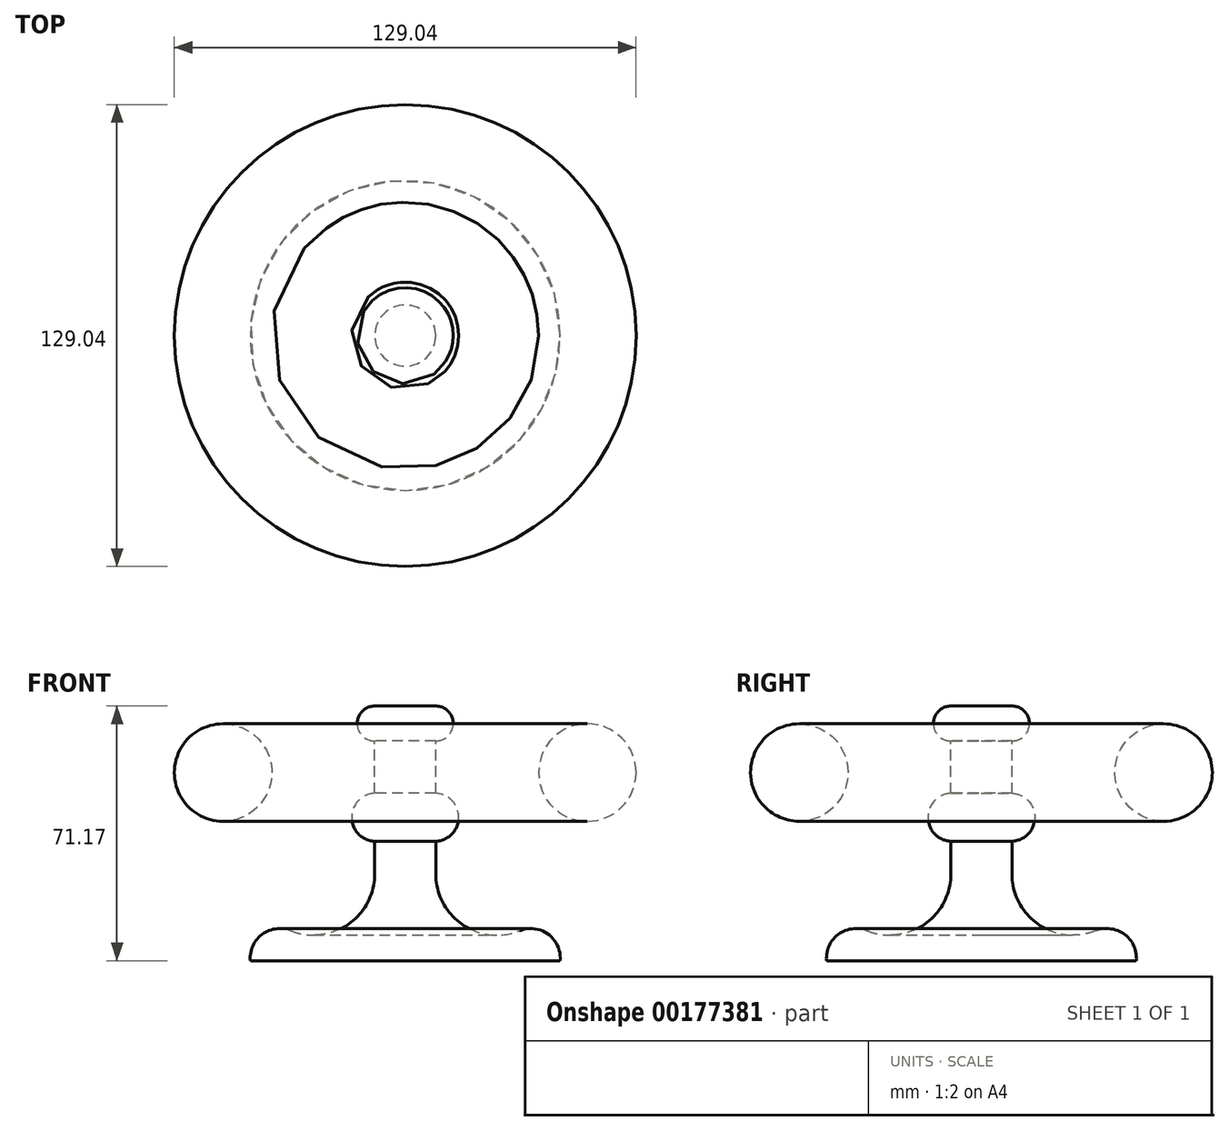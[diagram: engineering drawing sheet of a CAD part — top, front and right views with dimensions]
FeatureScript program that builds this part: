
annotation { "Feature Type Name" : "Feature", "Feature Type Description" : "" }
export const myFeature = defineFeature(function(context is Context, id is Id, definition is map)
    precondition{}
    {
        {
            var Q0;
            Q0=qCreatedBy(makeId("Front.planeOp"),FACE);
            var sketch = newSketch(context, id + "F0", { "sketchPlane" : qUnion([Q0])});
            skLineSegment(sketch, "E0", {"start": v(0, 71.17) * mm, "end": v(0, 0) * mm});
            skLineSegment(sketch, "E1", {"start": v(0, 0) * mm, "end": v(43.28, 0) * mm});
            skLineSegment(sketch, "E2", {"start": v(0, 71.17) * mm, "end": v(8.53, 71.17) * mm});
            skArc(sketch, "E3", {"start": v(8.53, 61.42) * mm, "mid": v(13.41, 66.3) * mm, "end": v(8.53, 71.17) * mm});
            skLineSegment(sketch, "E4", {"start": v(8.53, 61.42) * mm, "end": v(8.53, 46.79) * mm});
            skArc(sketch, "E5", {"start": v(8.53, 33.38) * mm, "mid": v(14.94, 40.08) * mm, "end": v(8.53, 46.79) * mm});
            skLineSegment(sketch, "E6", {"start": v(8.53, 33.38) * mm, "end": v(8.53, 24.23) * mm});
            skArc(sketch, "E7", {"start": v(8.53, 24.23) * mm, "mid": v(16.06, 10.07) * mm, "end": v(32, 8.38) * mm});
            skArc(sketch, "E8", {"start": v(32, 8.38) * mm, "mid": v(40, 7.35) * mm, "end": v(43.28, 0) * mm});
            skLineSegment(sketch, "E9", {"start": v(0, 97.69) * mm, "end": v(0, -25.15) * mm});
            skSolve(sketch);
        }
        {
            var Q0;
            Q0 = qSketchRegion(id + "F0", true);
            var Q1;
            Q1=sQuery(id+"F0.wireOp",EDGE,"E9");
            revolve(context, id + "F1", {"entities" : qUnion([Q0]), "axis" : qUnion([Q1]), "revolveType" : RevolveType.FULL});
        }
        {
            var Q0;
            Q0=qCreatedBy(makeId("Right.planeOp"),FACE);
            var sketch = newSketch(context, id + "F2", { "sketchPlane" : qUnion([Q0])});
            skCircle(sketch, "E10", {"center": v(-50.9, 52.58) * mm, "radius": 13.62 * mm});
            skLineSegment(sketch, "E11", {"start": v(0, 76.66) * mm, "end": v(0, -26.97) * mm});
            skSolve(sketch);
        }
        {
            var Q0;
            Q0 = qSketchRegion(id + "F2", true);
            var Q1;
            Q1=sQuery(id+"F2.wireOp",EDGE,"E11");
            revolve(context, id + "F3", {"entities" : qUnion([Q0]), "axis" : qUnion([Q1]), "revolveType" : RevolveType.FULL});
        }
    });
